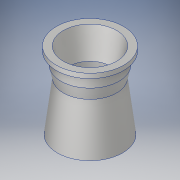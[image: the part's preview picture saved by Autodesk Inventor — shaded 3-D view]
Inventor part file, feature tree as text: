
AUTODESK INVENTOR PART (.ipt)
format: ipt  version: 2017 SP1 (Build 210196100, 196)  size: 177,152 bytes
history: native  units: in
note: dims shown in document units (in); Inventor stores cm internally (conversion verified against a paired STEP export)
features: revolve x1, sketch x1
ambient origin geometry x8: Origin, YZ Plane, XZ Plane, XY Plane, X Axis, Y Axis, Z Axis, Center Point
bodies: Body1 (feature_tree)
feature tree (2):
  revolve  "Revolution3"  [1 undecoded]
  sketch  "Sketch1"  dims[d0=1.13in d3=0.1718in d5=1.0in d6=1.0in d7=90.0deg d8=0.5in d9=15.0deg d31=0.25in d34=15.0deg d37=1.75in d40=3.75in d41=0.125in d46=0.75in d47=0.5in d51=0.5in d52=0.25in d54=0.5in d55=0.5in d56=1.25in d58=0.0017in d59=0.5in d60=0.5in d61=1.0in d62=0.234in d63=0.234in d64=0.125in d67=0.25in d68=4.25in d69=0.25in d70=0.25in d71=0.125in d73=3.4in d74=1.25in d75=0.2498in d77=90.0deg]
note: 1 required parameter value undecoded (feature->parameter linkage not recoverable at this tier; creation-order binding heuristic only, values carry confidence <= 0.55)
